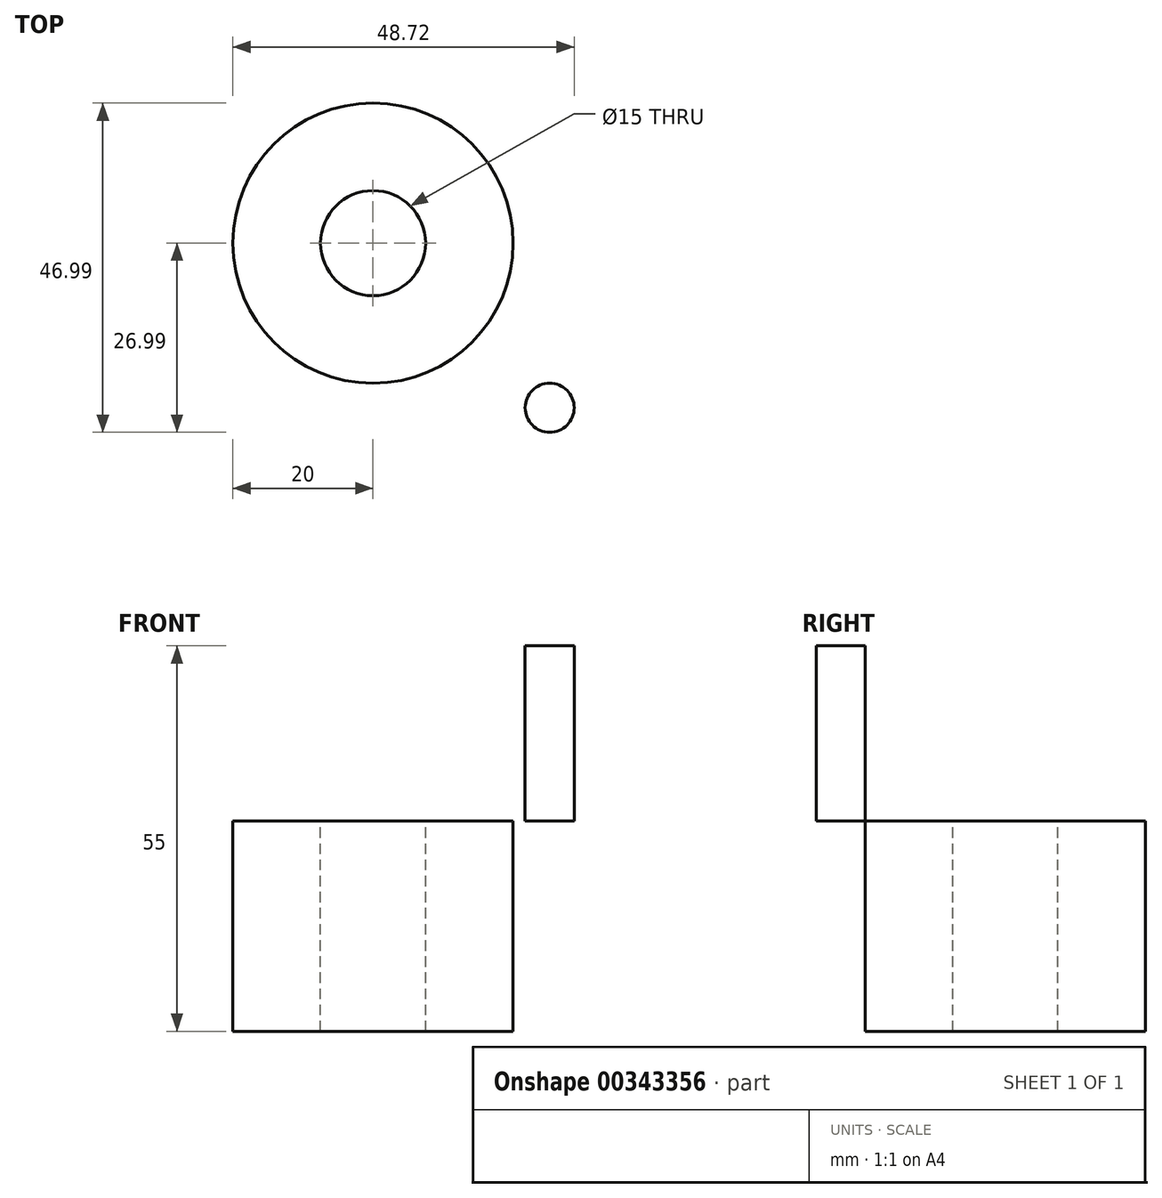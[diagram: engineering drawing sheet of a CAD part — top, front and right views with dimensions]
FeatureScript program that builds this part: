
annotation { "Feature Type Name" : "Feature", "Feature Type Description" : "" }
export const myFeature = defineFeature(function(context is Context, id is Id, definition is map)
    precondition{}
    {
        {
            var Q0;
            Q0=qCreatedBy(makeId("Top.planeOp"),FACE);
            var sketch = newSketch(context, id + "F0", { "sketchPlane" : qUnion([Q0])});
            skCircle(sketch, "E0", {"center": v(0, 0) * mm, "radius": 20 * mm});
            skSolve(sketch);
        }
        {
            var Q0;
            Q0=makeQuery(id+"F0.imprint","IMPRINT",FACE,{"disambiguationData":[TD([[makeQuery(id+"F0.imprint","IMPRINT",EDGE,{"derivedFrom":sQuery(id+"F0.wireOp",EDGE,"E0")}),1.0]])]});
            extrude(context, id + "F1", {"entities" : qUnion([Q0]), "depth" : 30 * mm});
        }
        {
            var Q0;
            Q0=makeQuery(id+"F1.opExtrude","CAP_FACE",FACE,{"disambiguationData":[OSD([sQuery(id+"F0.wireOp",EDGE,"E0")])],"isStart":false});
            var sketch = newSketch(context, id + "F2", { "sketchPlane" : qUnion([Q0])});
            skPoint(sketch, "E1", {"position": v(25.22, -23.5) * mm});
            skCircle(sketch, "E2", {"center": v(25.22, -23.5) * mm, "radius": 3.5 * mm});
            skSolve(sketch);
        }
        {
            var Q0;
            Q0=makeQuery(id+"F2.imprint","IMPRINT",FACE,{"disambiguationData":[TD([[makeQuery(id+"F2.imprint","IMPRINT",EDGE,{"derivedFrom":sQuery(id+"F2.wireOp",EDGE,"E2")}),1.0]])]});
            extrude(context, id + "F3", {"entities" : qUnion([Q0]), "depth" : 25 * mm});
        }
        {
            var Q0;
            Q0=makeQuery(id+"F1.opExtrude","CAP_FACE",FACE,{"disambiguationData":[OSD([sQuery(id+"F0.wireOp",EDGE,"E0")])],"isStart":false});
            var sketch = newSketch(context, id + "F4", { "sketchPlane" : qUnion([Q0])});
            skCircle(sketch, "E3", {"center": v(0, 0) * mm, "radius": 7.5 * mm});
            skSolve(sketch);
        }
        {
            var Q0;
            Q0=makeQuery(id+"F4.imprint","IMPRINT",FACE,{"disambiguationData":[TD([[makeQuery(id+"F4.imprint","IMPRINT",EDGE,{"derivedFrom":sQuery(id+"F4.wireOp",EDGE,"E3")}),1.0]])]});
            extrude(context, id + "F5", {"entities" : qUnion([Q0]), "operationType" : NewBodyOperationType.REMOVE, "endBound" : BoundingType.THROUGH_ALL, "oppositeDirection" : true, "depth" : 25 * mm});
        }
    });
